# Revit family: PRD_FrankeWS_WlHngUrnls_Urinal_HDTX538RS
name_source: partatom
category: Plumbing Fixtures
revit_build: Autodesk Revit 2018 (Build: 20190510_1515(x64)
units: mm (PartAtom-declared; Revit-internal decimal feet)

## family parameters
Cut with Voids When Loaded = No
Host = Face
OmniClass Number = 23.45.05.21.11.21
OmniClass Title = Urinals
Part Type = Normal
Room Calculation Point = No
Round Connector Dimension = Use Diameter
Shared = No

## types (1)
- HDTX538RS
    AssetType = Fixed
    BIMObjectName = PRD_AR_WallHungUrinals_Urinal_HDTX538RS
    Category = Pr_40_20_93_82, Wall-hung urinals
    Default Elevation = 650 mm  [stored 2.13255 ft]
    Description = Single urinal, hidden mounting with stainless steel rods through wall (service room behind needed), stainless steel, surface satin finished, material thickness 1.2 mm, oval bowl, hidden horizontal outlet towards wall, mounting and fixing conform to EN80, hidden screws, incl. wall fixing bolts. 4 liter flush. Products can be foam filled, on request, for extra strength and reduction of noise in a security environment. with stainless steel spreader 1/2inch, hidden mounting with stainless steel rods through wall and ring sensor
    DurationUnit = year
    Features = stainless steel, 1.20 mm, satin finished, wall mounting, 313x732x341 mm (WxHxD)
    Finish = Satin finished
    Form = Wall hung
    GrossWeight = 9.50 kg
    IfcExportAs = IfcSanitaryTerminalType
    IfcExportType = URINAL
    IntegralAccessories = Included wall fixing bolts
    Manufacturer = KWC Group AG
    ManufacturerName = KWC Group AG
    ManufacturerURL = www.kwc.com
    Material = PRD_AR_StainlessSteel_SatinFinished
    MaterialsBody = Stainless steel 1.4301
    MaterialsFinishAndColour = Stainless steel, satin finished
    Model = HDTX538RS
    ModelNumber = 2000103385
    ModelReference = HDTX538RS
    NBSDescription = Wall hung urinals
    NBSReference = 45-35-70/350
    Name = Urinal HDTX538RS
    NetWeight = 16.00 kg
    NominalDepth = 341 mm
    NominalHeight = 732 mm
    NominalLength = 732 mm
    NominalWidth = 313 mm  [stored 1.0269 ft]
    ProductInformation = https://pim.kwc.com
    Size = 313 x 732 x 341 mm
    SpilloverLevel = 650 mm  [stored 2.13255 ft]
    URL = www.kwc.com
    Uniclass2015Code = Pr_40_20_93_82
    Uniclass2015Title = Wall-hung urinals
    Uniclass2015Version = Products v1.7
    UrinalColor = Stainless steel
    UrinalMaterial = Stainless steel
    UrinalType = Bowl
    Version = 1
    WarrantyDurationUnit = year
    WasteSize = 50  [stored 0.164042 ft]
    WaterSupplyOverflowAndWasteHolesOverflow = None
    WaterSupplyOverflowAndWasteHolesWaste = Concealed
    WaterSupplyOverflowAndWasteHolesWaterSupply = Concealed

note: [stored X ft] marks values corroborated as IEEE doubles in the binary element streams (Revit-internal decimal feet)

## geometry (parser evidence)
native form markers: Sweep x3
no freeform markers — native parametric forms only
